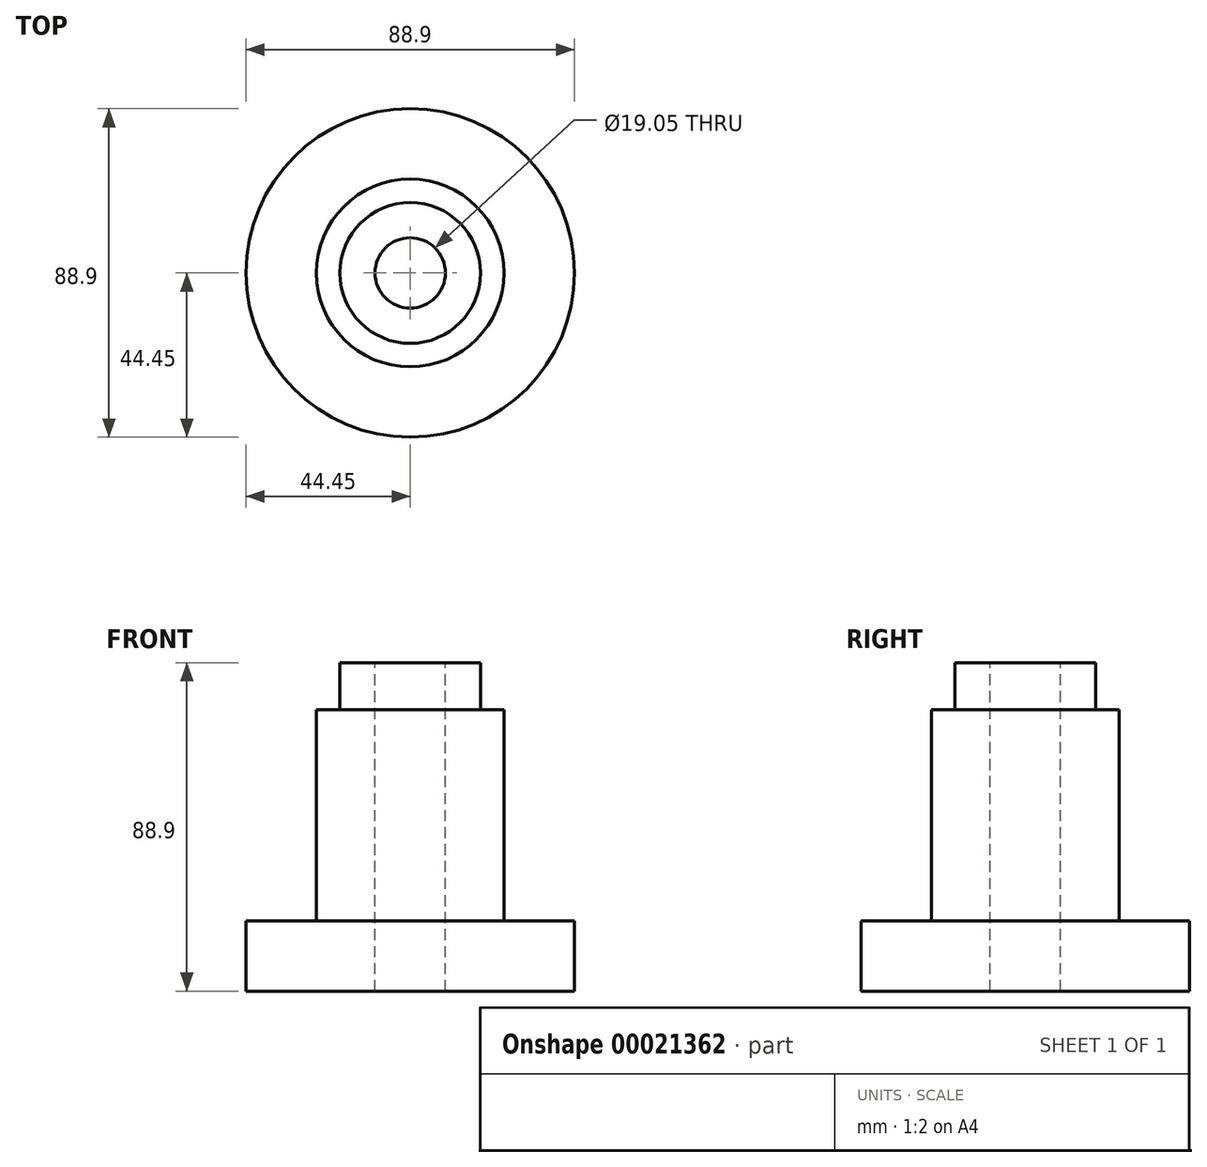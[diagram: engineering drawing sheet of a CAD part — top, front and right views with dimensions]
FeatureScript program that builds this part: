
annotation { "Feature Type Name" : "Feature", "Feature Type Description" : "" }
export const myFeature = defineFeature(function(context is Context, id is Id, definition is map)
    precondition{}
    {
        {
            var Q0;
            Q0=qCreatedBy(makeId("Front.planeOp"),FACE);
            var sketch = newSketch(context, id + "F0", { "sketchPlane" : qUnion([Q0])});
            skLineSegment(sketch, "E0.bottom", {"start": v(-44.45, -10.43) * mm, "end": v(0, -10.43) * mm});
            skLineSegment(sketch, "E0.top", {"start": v(-44.45, 8.62) * mm, "end": v(0, 8.62) * mm});
            skLineSegment(sketch, "E0.left", {"start": v(-44.45, -10.43) * mm, "end": v(-44.45, 8.62) * mm});
            skLineSegment(sketch, "E0.right", {"start": v(0, -10.43) * mm, "end": v(0, 8.62) * mm});
            skLineSegment(sketch, "E1", {"start": v(-25.4, 8.62) * mm, "end": v(-25.4, 65.77) * mm});
            skLineSegment(sketch, "E2", {"start": v(-25.4, 65.77) * mm, "end": v(0, 65.77) * mm});
            skLineSegment(sketch, "E3", {"start": v(0, 65.77) * mm, "end": v(0, 8.62) * mm});
            skLineSegment(sketch, "E4", {"start": v(-19.05, 65.77) * mm, "end": v(-19.05, 78.47) * mm});
            skLineSegment(sketch, "E5", {"start": v(-19.05, 78.47) * mm, "end": v(0, 78.47) * mm});
            skLineSegment(sketch, "E6", {"start": v(0, 78.47) * mm, "end": v(0, 65.77) * mm});
            skSolve(sketch);
        }
        {
            var Q0;
            Q0=makeQuery(id+"F0.imprint","IMPRINT",FACE,{"disambiguationData":[TD([[makeQuery(id+"F0.imprint","IMPRINT",EDGE,{"derivedFrom":sQuery(id+"F0.wireOp",EDGE,"E0.bottom")}),1.0]])]});
            var Q1;
            {var subQ1=sQuery(id+"F0.wireOp",EDGE,"E1");Q1=makeQuery(id+"F0.imprint","IMPRINT",FACE,{"disambiguationData":[TD([[makeQuery(id+"F0.imprint","IMPRINT",EDGE,{"derivedFrom":subQ1}),-1.0]])]});}
            var Q2;
            {var subQ1=sQuery(id+"F0.wireOp",EDGE,"E4");Q2=makeQuery(id+"F0.imprint","IMPRINT",FACE,{"disambiguationData":[TD([[makeQuery(id+"F0.imprint","IMPRINT",EDGE,{"derivedFrom":subQ1}),-1.0]])]});}
            var Q3;
            Q3=sQuery(id+"F0.wireOp",EDGE,"E0.right");
            revolve(context, id + "F1", {"entities" : qUnion([Q0, Q1, Q2]), "axis" : qUnion([Q3]), "revolveType" : RevolveType.FULL});
        }
        {
            var Q0;
            Q0=makeQuery(id+"F1.opRevolve","SWEPT_FACE",FACE,{"disambiguationData":[OSD([sQuery(id+"F0.wireOp",EDGE,"E5")])]});
            var sketch = newSketch(context, id + "F2", { "sketchPlane" : qUnion([Q0])});
            skCircle(sketch, "E7", {"center": v(0, 0) * mm, "radius": 9.53 * mm});
            skSolve(sketch);
        }
        {
            var Q0;
            Q0=makeQuery(id+"F2.imprint","IMPRINT",FACE,{"disambiguationData":[TD([[makeQuery(id+"F2.imprint","IMPRINT",EDGE,{"derivedFrom":sQuery(id+"F2.wireOp",EDGE,"E7")}),1.0]])]});
            var Q1;
            Q1=sQuery(id+"F2.wireOp",EDGE,"E7");
            extrude(context, id + "F3", {"entities" : qUnion([Q0]), "operationType" : NewBodyOperationType.REMOVE, "surfaceEntities" : qUnion([Q1]), "oppositeDirection" : true, "depth" : 88.9 * mm});
        }
    });
